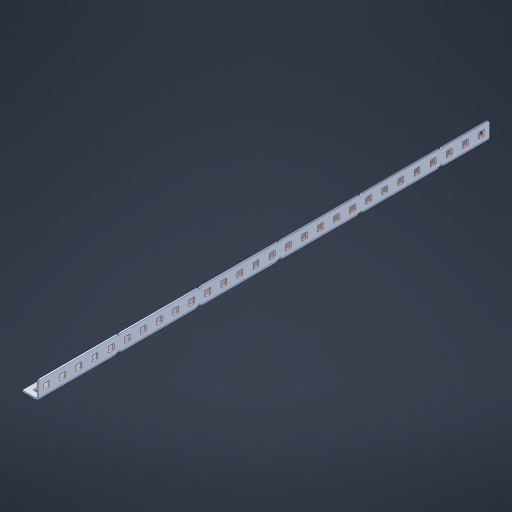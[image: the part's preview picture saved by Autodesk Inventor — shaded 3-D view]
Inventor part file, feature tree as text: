
AUTODESK INVENTOR PART (.ipt)
format: ipt  version: 2023 (Build 270158000, 158)  size: 904,704 bytes
history: native  units: in
note: dims shown in document units (in); Inventor stores cm internally (conversion verified against a paired STEP export)
features: other x61, extrude x55, sheet_metal_op x10, sketch x8, mirror x1, pattern_linear x1, chamfer x1
ambient origin geometry x8: Origin, YZ Plane, XZ Plane, XY Plane, X Axis, Y Axis, Z Axis, Center Point
bodies: Solid1 (feature_tree), Body (feature_tree)
feature tree (137):
  other  "Flange Pattern Plane"
  sheet_metal_op  "Flange Pattern"
  sheet_metal_op  "Body Pattern"
  other  "Arc Length"
  mirror  "Notch Mirror"
  pattern_linear  "Notch Pattern"  Spacing1=0.1875in  [1 undecoded]
  chamfer  "End Chamfer"
  extrude  "Half Cut"  Depth=0.0469in
  sketch  "Sketch1"  dims[d0=2.5in]
  other  "Plate1"
  sketch  "Sketch2"  dims[d1=14.0in]
  other  "Plate2"
  sheet_metal_op  "Bend1"
  sheet_metal_op  "Corner1"
  sketch  "Sketch3"  dims[d2=0.0469in]
  other  "Flange Pattern Sketch"
  sketch  "Sketch7"  dims[d3=0.0469in]
  other  "Srf1"
  other  "Srf2"
  sketch  "Sketch8"  dims[d4=0.0234in]
  sketch  "Sketch9"  dims[d5=0.0938in]
  other  "Srf91"
  sheet_metal_op  "Body Pattern Sketch"
  other  "Srf92"
  sketch  "Sketch13"  dims[d6=0.0469in]
  sketch  "Sketch14"  dims[d7=0.5in d8=90.0deg d9=0.0312in d10=0.1875in d11=0.0469in d12=0.0469in d16=0.182in d17=0.02in d18=0.0469in d19=0.0in d20=0.25in d21=0.25in d46=0.172in d47=1.0in d48=0.0in d49=0.182in d50=0.02in d51=0.25in d52=0.25in d53=0.0469in d54=0.0in d55=0.172in d56=1.0in d57=0.0in d60=11.0236in d62=0.5in d63=0.3937in d65=0.5in d85=0.1227in d86=0.1659in d88=0.04in d89=0.0469in d90=0.0in d91=0.04in d92=0.0491in d95=2.5in d96=0.04in d97=0.25in d98=45.0deg d101=0.0in d102=2.497in d131=0.5in d132=11.0236in d134=0.5in d139=0.5in]
  other  "Srf856"
  other  "Srf1310"
  other  "Srf1311"
  other  "Srf1312"
  other  "Srf1376"
  other  "Srf1377"
  other  "Srf1728"
  other  "Srf1755"
  other  "Srf1878"
  other  "Srf1879"
  other  "Srf1880"
  other  "Srf1881"
  other  "Srf1882"
  other  "Srf1883"
  other  "Srf1884"
  other  "Srf1885"
  other  "Srf1886"
  other  "Srf1887"
  other  "Srf1888"
  other  "Srf1889"
  other  "Srf1890"
  other  "Srf1891"
  other  "Srf1892"
  other  "Srf1893"
  other  "Srf1894"
  other  "Srf1895"
  other  "Srf1896"
  other  "Srf1897"
  other  "Srf1898"
  other  "Srf1899"
  other  "Srf1942"
  other  "Srf1943"
  other  "Srf1944"
  other  "Srf1945"
  other  "Srf1946"
  other  "Srf1947"
  other  "Srf1948"
  other  "Srf1949"
  other  "Srf1950"
  other  "Srf1951"
  other  "Srf1952"
  other  "Srf1953"
  other  "Srf1954"
  other  "Srf1955"
  other  "Srf1956"
  other  "Srf1957"
  other  "Srf1958"
  other  "Srf1959"
  other  "Srf1960"
  other  "Srf1961"
  other  "Srf1962"
  other  "Srf1963"
  sheet_metal_op  "Flange Stamp"
  sheet_metal_op  "Flange Circle"
  sheet_metal_op  "Body Stamp"
  sheet_metal_op  "Body Circle"
  sheet_metal_op  "Notch"
  extrude  "ExtrusionSrf2"  Depth=0.0469in
  extrude  "ExtrusionSrf92"  Depth=0.5in
  extrude  "ExtrusionSrf856"  Depth=0.02in
  extrude  "ExtrusionSrf1310"  Depth=0.0469in
  extrude  "ExtrusionSrf1311"  TaperAngle=0.0deg  [1 undecoded]
  extrude  "ExtrusionSrf1312"  Depth=0.5in
  extrude  "ExtrusionSrf1376"  Depth=0.5in
  extrude  "ExtrusionSrf1377"  Depth=0.5in
  extrude  "ExtrusionSrf1728"  Depth=0.5in TaperAngle=0.0deg
  extrude  "ExtrusionSrf1755"  Depth=0.5in
  extrude  "ExtrusionSrf1878"  Depth=0.02in
  extrude  "ExtrusionSrf1879"  Depth=0.5in
  extrude  "ExtrusionSrf1880"  Depth=0.5in
  extrude  "ExtrusionSrf1881"  Depth=0.0469in
  extrude  "ExtrusionSrf1882"  TaperAngle=0.0deg  [1 undecoded]
  extrude  "ExtrusionSrf1883"  Depth=0.5in
  extrude  "ExtrusionSrf1884"  Depth=0.5in TaperAngle=0.0deg
  extrude  "ExtrusionSrf1885"  Depth=0.5in
  extrude  "ExtrusionSrf1886"  Depth=0.5in
  extrude  "ExtrusionSrf1887"  Depth=0.5in
  extrude  "ExtrusionSrf1888"  Depth=0.5in
  extrude  "ExtrusionSrf1889"  Depth=0.5in
  extrude  "ExtrusionSrf1890"  Depth=0.0469in
  extrude  "ExtrusionSrf1891"  TaperAngle=0.0deg  [1 undecoded]
  extrude  "ExtrusionSrf1892"  Depth=0.5in
  extrude  "ExtrusionSrf1893"  Depth=0.5in
  extrude  "ExtrusionSrf1894"  Depth=0.5in
  extrude  "ExtrusionSrf1895"  Depth=0.5in TaperAngle=45.0deg
  extrude  "ExtrusionSrf1896"  TaperAngle=0.0deg  [1 undecoded]
  extrude  "ExtrusionSrf1897"  Depth=0.5in
  extrude  "ExtrusionSrf1898"  Depth=0.5in
  extrude  "ExtrusionSrf1899"  Depth=0.5in
  extrude  "ExtrusionSrf1942"  Depth=0.5in
  extrude  "ExtrusionSrf1943"  Depth=0.5in
  extrude  "ExtrusionSrf1944"  [1 undecoded]
  extrude  "ExtrusionSrf1945"  [1 undecoded]
  extrude  "ExtrusionSrf1946"  [1 undecoded]
  extrude  "ExtrusionSrf1947"  [1 undecoded]
  extrude  "ExtrusionSrf1948"  [1 undecoded]
  extrude  "ExtrusionSrf1949"  [1 undecoded]
  extrude  "ExtrusionSrf1950"  [1 undecoded]
  extrude  "ExtrusionSrf1951"  [1 undecoded]
  extrude  "ExtrusionSrf1952"  [1 undecoded]
  extrude  "ExtrusionSrf1953"  [1 undecoded]
  extrude  "ExtrusionSrf1954"  [1 undecoded]
  extrude  "ExtrusionSrf1955"  [1 undecoded]
  extrude  "ExtrusionSrf1956"  [1 undecoded]
  extrude  "ExtrusionSrf1957"  [1 undecoded]
  extrude  "ExtrusionSrf1958"  [1 undecoded]
  extrude  "ExtrusionSrf1959"  [1 undecoded]
  extrude  "ExtrusionSrf1960"  [1 undecoded]
  extrude  "ExtrusionSrf1961"  [1 undecoded]
  extrude  "ExtrusionSrf1962"  [1 undecoded]
  extrude  "ExtrusionSrf1963"  [1 undecoded]
note: 25 required parameter values undecoded (feature->parameter linkage not recoverable at this tier; creation-order binding heuristic only, values carry confidence <= 0.55)
